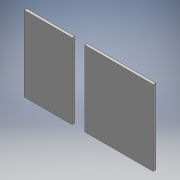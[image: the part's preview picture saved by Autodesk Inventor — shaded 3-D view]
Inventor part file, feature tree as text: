
AUTODESK INVENTOR PART (.ipt)
format: ipt  version: 2016 (Build 200138000, 138)  size: 94,208 bytes
history: native  units: mm
features: extrude x1
ambient origin geometry x8: Origin, YZ Plane, XZ Plane, XY Plane, X Axis, Y Axis, Z Axis, Center Point
bodies: Body1 (feature_tree)
feature tree (1):
  extrude  "Extrusion2"  Depth=10.0mm
